# Revit family: Table-Casual-Teknion-ATCCB-Circular_Bistro-R2015
name_source: partatom
category: Furniture
revit_build: Autodesk Revit Architecture 2015 (Build: 20140323_1530(x64)
units: mm (PartAtom-declared; Revit-internal decimal feet)

## types (2) — shared parameters
Assembly Code = E2020200
Description = Circular Bistro Table
Height = 29 "
Manufacturer = Teknion
Manufacturer Fax = 416.661.4586
Part Number = ATCCB
Product Documentation Link = http://www.teknion.com
Product Line = Tables & Collaborative Spaces
Product Page URL = http://www.teknion.com
Series = Tables & Collaborative Spaces
Sustainability Data = http://www.teknion.com
URL = www.teknion.com
Unit Weight URL = http://www.teknion.com
Warranty = http://www.teknion.com

## per-type parameters (varying)
| type | Diameter | Model | Radius |
| 24" Diameter | 24 " | ATCCB24 | 12 " |
| 30" Diameter | 30 " | ATCCB30 | 15 " |

## geometry (parser evidence)
native form markers: Blend x2, Sweep x2
no freeform markers — native parametric forms only
